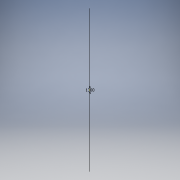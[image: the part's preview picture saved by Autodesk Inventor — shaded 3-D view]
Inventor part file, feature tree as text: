
AUTODESK INVENTOR PART (.ipt)
format: ipt  version: 2016 (Build 200138000, 138)  size: 80,384 bytes
history: native  units: mm
features: sketch x1
ambient origin geometry x8: Origin, YZ Plane, XZ Plane, XY Plane, X Axis, Y Axis, Z Axis, Center Point
feature tree (1):
  sketch  "Sketch1"  dims[d0=1040.0mm]
